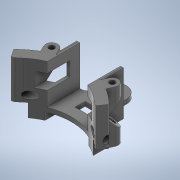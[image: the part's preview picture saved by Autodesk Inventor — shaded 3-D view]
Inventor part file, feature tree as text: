
AUTODESK INVENTOR PART (.ipt)
format: ipt  version: 2020 (Build 240168000, 168)  size: 1,243,648 bytes
history: native  units: mm
features: projected_geometry x61, extrude x30, sketch x30, other x11, chamfer x5, fillet x3, sweep x1
ambient origin geometry x8: Origin, YZ Plane, XZ Plane, XY Plane, X Axis, Y Axis, Z Axis, Center Point
bodies: Body1 (feature_tree)
feature tree (141):
  other  "Твердое тело1"
  extrude  "Выдавливание1"  Depth=35.0mm TaperAngle=0.0deg
  sketch  "Эскиз2"
  extrude  "Выдавливание2"  Depth=4.0mm
  sweep  "Сдвиг1"
  extrude  "Выдавливание5"  Depth=8.0mm
  extrude  "Выдавливание6"  Depth=35.0mm TaperAngle=0.0deg
  extrude  "Выдавливание7"  Depth=8.5mm
  extrude  "Выдавливание8"  TaperAngle=45.0deg  [1 undecoded]
  other  "РабПлоскость1"
  extrude  "Выдавливание9"  Depth=8.5mm
  extrude  "Выдавливание10"  TaperAngle=45.0deg  [1 undecoded]
  extrude  "Выдавливание11"  TaperAngle=0.0deg  [1 undecoded]
  sketch  "Эскиз13"
  other  "РабПлоскость2"
  sketch  "Эскиз14"
  extrude  "Выдавливание12"  Depth=5.0mm TaperAngle=0.0deg
  extrude  "Выдавливание13"  Depth=15.0mm TaperAngle=0.0deg
  other  "РабПлоскость3"
  extrude  "Выдавливание14"  Depth=15.0mm TaperAngle=0.0deg
  extrude  "Выдавливание15"  Depth=26.0mm
  extrude  "Выдавливание16"  Depth=6.0mm
  extrude  "Выдавливание17"  Depth=15.0mm TaperAngle=0.0deg
  chamfer  "Фаска1"  Distance=2.0mm
  other  "РабПлоскость4"
  sketch  "Эскиз18"
  extrude  "Выдавливание18"  Depth=1.5mm
  extrude  "Выдавливание19"  Depth=3.0mm
  extrude  "Выдавливание20"  Depth=6.0mm
  chamfer  "Фаска2"  Distance=2.5mm
  fillet  "Сопряжение1"  [1 undecoded]
  extrude  "Выдавливание21"  Depth=15.0mm TaperAngle=0.0deg
  extrude  "Выдавливание22"  Depth=10.0mm TaperAngle=0.0deg
  extrude  "Выдавливание23"  Depth=7.0mm TaperAngle=0.0deg
  other  "РабПлоскость5"
  extrude  "Выдавливание24"  Depth=40.0mm
  chamfer  "Фаска3"  Distance=3.8mm
  sketch  "Эскиз24"
  other  "РабПлоскость6"
  extrude  "Выдавливание25"  TaperAngle=0.0deg  [1 undecoded]
  sketch  "Эскиз26"
  other  "РабПлоскость7"
  sketch  "Эскиз27"
  extrude  "Выдавливание26"  Depth=16.5mm
  extrude  "Выдавливание27"  Depth=25.5mm
  extrude  "Выдавливание28"  Depth=2.3mm
  chamfer  "Фаска4"  Distance=3.0mm
  other  "РабПлоскость8"
  extrude  "Выдавливание29"  Depth=7.0mm
  other  "РабПлоскость9"
  extrude  "Выдавливание30"  Depth=18.0mm
  chamfer  "Фаска5"  Distance=1.5mm
  fillet  "Сопряжение2"  Radius=4.5mm
  fillet  "Сопряжение3"  Radius=6.5mm
  other  "РабПлоскость10"
  extrude  "Выдавливание31"  Depth=3.5mm
  extrude  "Выдавливание32"  Depth=1.0mm
  sketch  "Эскиз1"
  sketch  "Эскиз3"
  projected_geometry  "Спроецированная петля1"
  projected_geometry  "Спроецированная петля2"
  sketch  "3D эскиз1"
  sketch  "Эскиз4"
  sketch  "Эскиз6"
  projected_geometry  "Спроецированная петля4"
  sketch  "Эскиз7"
  projected_geometry  "Спроецированная петля5"
  sketch  "Эскиз9"
  projected_geometry  "Спроецированная петля7"
  sketch  "Эскиз11"
  projected_geometry  "Спроецированная петля8"
  sketch  "Эскиз12"
  projected_geometry  "Спроецированная петля9"
  projected_geometry  "Спроецированная петля10"
  sketch  "Эскиз15"
  sketch  "Эскиз16"
  projected_geometry  "Спроецированная петля11"
  projected_geometry  "Спроецированная петля12"
  sketch  "Эскиз17"
  projected_geometry  "Спроецированная петля13"
  projected_geometry  "Спроецированная петля14"
  projected_geometry  "Спроецированная петля15"
  projected_geometry  "Спроецированная петля16"
  sketch  "Эскиз19"
  projected_geometry  "Спроецированная петля17"
  sketch  "Эскиз20"
  projected_geometry  "Спроецированная петля18"
  projected_geometry  "Спроецированная петля19"
  projected_geometry  "Спроецированная петля20"
  projected_geometry  "Спроецированная петля21"
  projected_geometry  "Спроецированная петля22"
  projected_geometry  "Спроецированная петля23"
  sketch  "Эскиз21"
  projected_geometry  "Спроецированная петля24"
  projected_geometry  "Спроецированная петля25"
  projected_geometry  "Спроецированная петля26"
  projected_geometry  "Спроецированная петля27"
  projected_geometry  "Спроецированная петля28"
  projected_geometry  "Спроецированная петля29"
  projected_geometry  "Спроецированная петля30"
  projected_geometry  "Спроецированная петля31"
  sketch  "Эскиз22"
  projected_geometry  "Спроецированная петля32"
  projected_geometry  "Спроецированная петля33"
  sketch  "Эскиз23"
  projected_geometry  "Спроецированная петля34"
  projected_geometry  "Спроецированная петля35"
  projected_geometry  "Спроецированная петля36"
  projected_geometry  "Спроецированная петля37"
  sketch  "Эскиз25"
  projected_geometry  "Спроецированная петля38"
  projected_geometry  "Спроецированная петля39"
  projected_geometry  "Спроецированная петля40"
  projected_geometry  "Спроецированная петля41"
  projected_geometry  "Спроецированная петля42"
  projected_geometry  "Спроецированная петля43"
  projected_geometry  "Спроецированная петля44"
  projected_geometry  "Спроецированная петля45"
  projected_geometry  "Спроецированная петля46"
  projected_geometry  "Спроецированная петля47"
  projected_geometry  "Спроецированная петля48"
  projected_geometry  "Спроецированная петля49"
  sketch  "Эскиз28"
  projected_geometry  "Спроецированная петля50"
  projected_geometry  "Спроецированная петля51"
  projected_geometry  "Спроецированная петля52"
  projected_geometry  "Спроецированная петля53"
  projected_geometry  "Спроецированная петля54"
  sketch  "Эскиз29"
  sketch  "Эскиз30"
  projected_geometry  "Спроецированная петля55"
  projected_geometry  "Спроецированная петля56"
  sketch  "Эскиз31"
  projected_geometry  "Спроецированная петля57"
  sketch  "Эскиз32"
  projected_geometry  "Спроецированная петля58"
  projected_geometry  "Спроецированная петля59"
  projected_geometry  "Спроецированная петля60"
  projected_geometry  "Спроецированная петля61"
  projected_geometry  "Спроецированная петля62"
  projected_geometry  "Спроецированная петля63"
note: 5 required parameter values undecoded (feature->parameter linkage not recoverable at this tier; creation-order binding heuristic only, values carry confidence <= 0.55)
